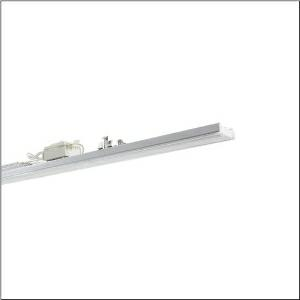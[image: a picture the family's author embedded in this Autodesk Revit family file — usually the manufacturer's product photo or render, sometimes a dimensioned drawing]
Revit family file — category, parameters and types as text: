
# Revit family: licross_r__11_recessed_mo_51tl12dv4fxg3s4_4c8e
name_source: partatom
category: Lighting Fixtures
units: mm (PartAtom-declared; Revit-internal decimal feet)

## family parameters
Cut with Voids When Loaded = No
Host = Face
Light Source = No
Part Type = Normal
Room Calculation Point = No
Round Connector Dimension = Use Diameter
Shared = No

## types (1)
- --- (1 x LED, 1010 lm, 5.5 W, 4000K)
    Apparent Load = 6 VA
    CIE Flux Codes = 67 92 99 100 100
    Color Rendering = 80
    Color Temperature = 4000K
    Default Elevation = 1800 mm
    Description = Licross® 11 Recessed MO, luminaire insert, of sheet steel, coil coated, white, length: 2.250mm, width: 66mm, height: 67mm, LED rated luminous flux: 15.360lm, light colour: 840, control gear: DALI 2, with plug, 6-pole, with phase selection, for trunking rail, 9 or 11-core, mains connection: 220..240V, AC, 50/60Hz, rated input power: 88W, for trunking rail, 9-/11-core, internal wiring halogen-free, for emergency light function, converter,control gear: single battery element, battery: LiFePO4, 9Ah, primary optical cover: cover, of PMMA, light emission: direct distribution, primary light characteristic: symmetric, protection rating (complete): IP40, insulation class (complete): insulation class I (protective earthing), certification: CE, UKCA, protection symbol: D if used in an environment without relevant dust loads with corresponding accessories, impact resistance: IK06, permissible ambient temperature for indoor applications: +5..+35°C, standard: EN 60598-2-22, LABS conformity tested according to VDMA 24364:2018-05, reducing of maximum allowable ambient temperature of 5°C with ceiling mounting, corresponds to IFS (International Featured Standards) requirements for safety and quality in the food industry, packaging unit: 1 piece
    Height = 58 mm
    Lamp = 1 x LED
    Lamp Light Flux = 1010 lm
    Lamp Power = 5.5 W
    Lamp count = 1
    Length = 2250 mm
    Luminous efficacy = 184 lm/W
    Manufacturer = Siteco
    ModVariant = No
    Model = 51TL12DV4FXG3S4
    Mounting Place = Ceiling
    Mounting Type = Pendant
    Number of Poles = 1
    OnlyDefault = Yes
    Power Factor = 1
    Product Name = Licross® 11 Recessed MO
    Product group = luminaire insert | ceiling pendant
    ProductGroupID = 902
    Protection Class = Protection class I
    Protection Degree = IP 40
    RLX_Detail_Level = 1
    RLX_Emergency_Light_Flux = 0 lm
    RLX_Emergency_Type = 0
    RLX_Emergency_Type_DB = No
    RlxData = <blob elided: 29657 chars, md5=f56d4a46>
    Socket = socket
    Standby Power = 0 W
    System Light Flux = 1010 lm
    System Power = 6 W
    Type Comments = : emergency light operation: 3 h
    Type Image = l_1296930.jpg
    URL = http://relux.com
    VarID = @adj_106793
    Voltage = 0 V
    Weight = 0.00 kg
    Width = 66 mm

## geometry (parser evidence)
native form markers: Blend x4, Sweep x9
no freeform markers — native parametric forms only
